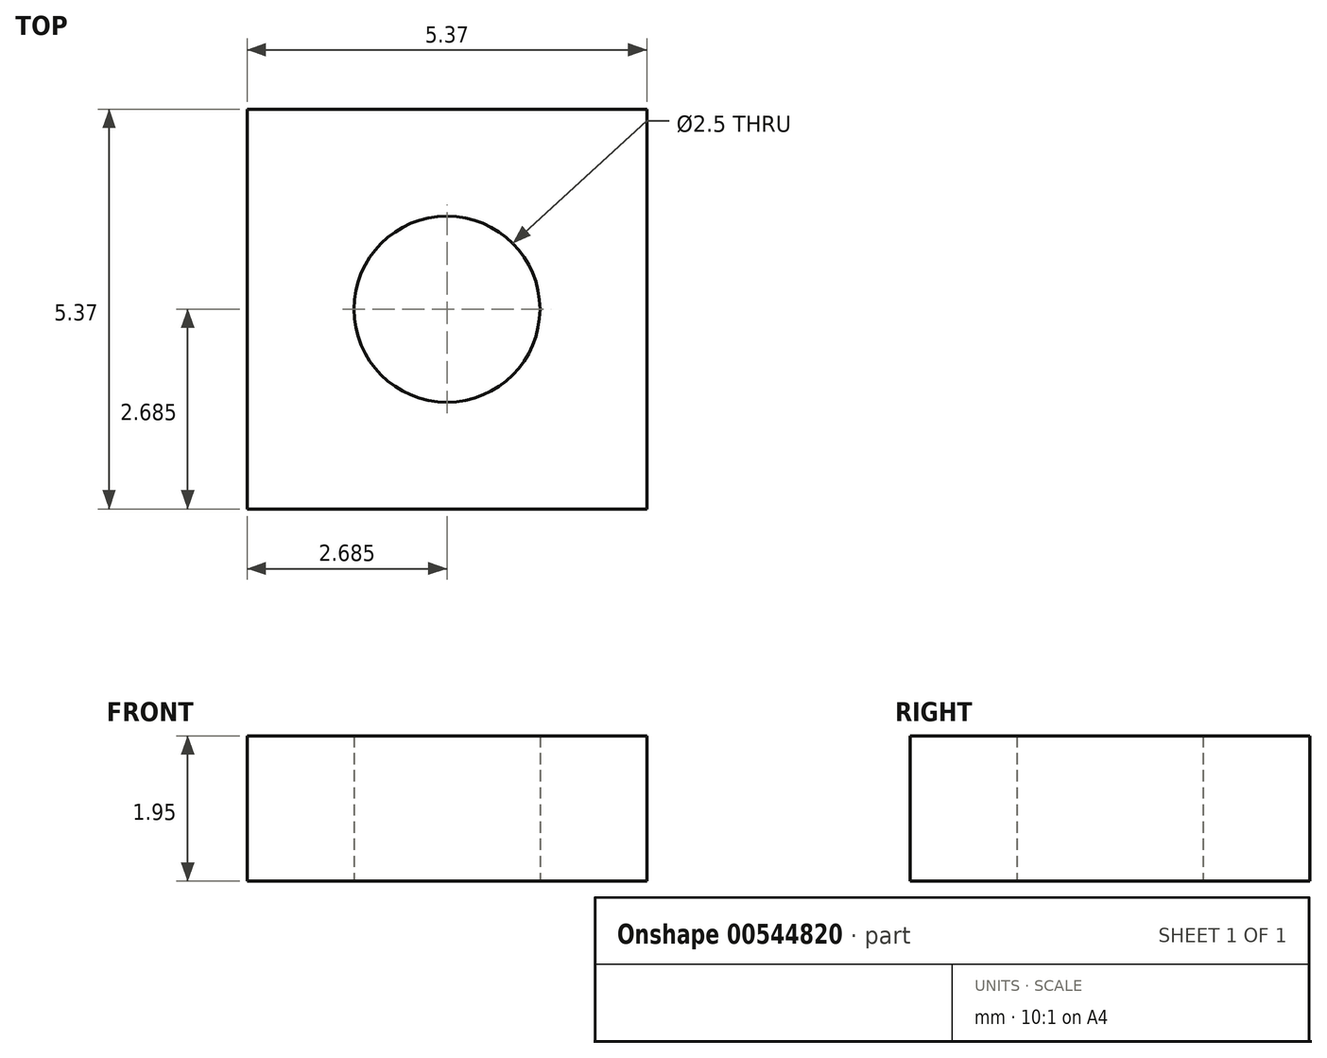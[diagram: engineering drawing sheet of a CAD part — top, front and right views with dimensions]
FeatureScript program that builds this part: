
annotation { "Feature Type Name" : "Feature", "Feature Type Description" : "" }
export const myFeature = defineFeature(function(context is Context, id is Id, definition is map)
    precondition{}
    {
        {
            var Q0;
            Q0=qCreatedBy(makeId("Top.planeOp"),FACE);
            var sketch = newSketch(context, id + "F0", { "sketchPlane" : qUnion([Q0])});
            skLineSegment(sketch, "E0.bottom", {"start": v(0, 0) * mm, "end": v(5.37, 0) * mm});
            skLineSegment(sketch, "E0.top", {"start": v(0, 5.37) * mm, "end": v(5.37, 5.37) * mm});
            skLineSegment(sketch, "E0.left", {"start": v(0, 0) * mm, "end": v(0, 5.37) * mm});
            skLineSegment(sketch, "E0.right", {"start": v(5.37, 0) * mm, "end": v(5.37, 5.37) * mm});
            skCircle(sketch, "E1", {"center": v(2.69, 2.69) * mm, "radius": 1.25 * mm});
            skPoint(sketch, "E1.centerSnap0", {"position": v(5.37, 2.69) * mm});
            skPoint(sketch, "E1.centerSnap1", {"position": v(2.69, 5.37) * mm});
            skSolve(sketch);
        }
        {
            var Q0;
            Q0 = qSketchRegion(id + "F0", true);
            extrude(context, id + "F1", {"entities" : qUnion([Q0]), "depth" : 1.95 * mm, "offsetDistance" : 25 * mm});
        }
    });
